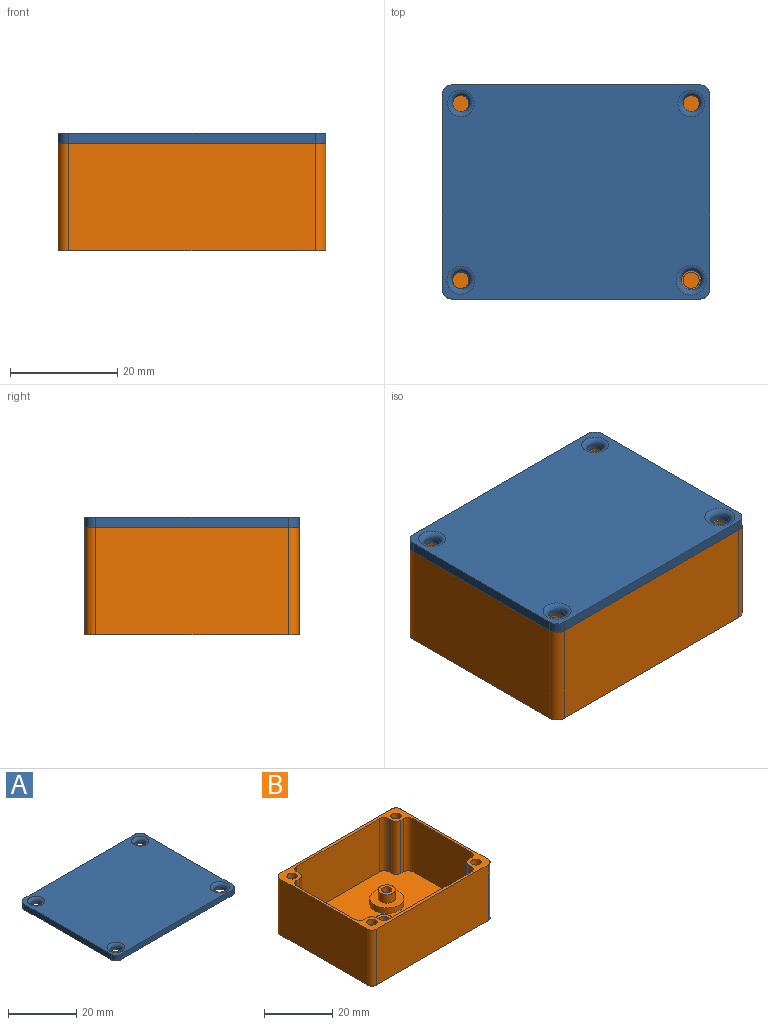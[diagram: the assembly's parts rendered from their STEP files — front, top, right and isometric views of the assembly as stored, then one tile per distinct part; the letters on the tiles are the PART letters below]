
ASSEMBLY  parts=2 mates=1
PART A: 18 faces, bbox 50x40x2 mm
  f0: plane 36x2mm, normal (-1,0,0), area 72mm2, adj f4,f5,f14,f17
  f1: plane 46x2mm, normal (0,-1,0), area 92mm2, adj f4,f5,f14,f15
  f2: plane 36x2mm, normal (1,0,0), area 72mm2, adj f4,f5,f15,f16
  f3: plane 46x2mm, normal (0,1,0), area 92mm2, adj f4,f5,f16,f17
  f4: plane 50x40mm, normal (0,0,1), area 1911mm2, adj f0,f1,f2,f3,f10,f11,f12,f13
  f5: plane 50x40mm, normal (0,0,-1), area 1964mm2, adj f0,f1,f2,f3,f6,f7,f8,f9
  f6: cylinder r=1.5mm len=3mm, axis (0,0,1), area 9.4mm2, adj f5,f13
  f7: cylinder r=1.5mm len=3mm, axis (0,0,1), area 9.4mm2, adj f5,f12
  f8: cylinder r=1.81mm len=3.62mm, axis (0,0,1), area 11.4mm2, adj f5,f11
  f9: cylinder r=1.62mm len=3.23mm, axis (0,0,1), area 10.2mm2, adj f5,f10
  f10: torus R=2.62mm, axis (0,0,1), area 19.5mm2, adj f4,f9
  f11: torus R=2.81mm, axis (0,0,1), area 21.4mm2, adj f4,f8
  f12: torus R=2.5mm, axis (0,0,1), area 18.4mm2, adj f4,f7
  f13: torus R=2.5mm, axis (0,0,1), area 18.4mm2, adj f4,f6
  f14: cylinder r=2mm len=2mm, axis (0,0,-1), area 6.3mm2, adj f0,f1,f4,f5
  f15: cylinder r=2mm len=2mm, axis (0,0,1), area 6.3mm2, adj f1,f2,f4,f5
  f16: cylinder r=2mm len=2mm, axis (0,0,-1), area 6.3mm2, adj f2,f3,f4,f5
  f17: cylinder r=2mm len=2mm, axis (0,0,1), area 6.3mm2, adj f0,f3,f4,f5
PART B: 67 faces, bbox 50x40x20 mm
  f0: cylinder r=1.5mm len=4mm, axis (0,0,-1), area 37.7mm2, adj f30,f50
  f1: cylinder r=1.5mm len=4mm, axis (0,0,-1), area 37.7mm2, adj f32,f43
  f2: plane 48x38mm, normal (0,0,1), area 1563.5mm2, adj f3,f4,f5,f6,f13,f14,f15,f16
  f3: plane 24x19mm, normal (-1,0,0), area 456mm2, adj f2,f7,f60,f61
  f4: plane 34x19mm, normal (0,1,0), area 646mm2, adj f2,f7,f56,f58
  f5: plane 34x19mm, normal (0,-1,0), area 646mm2, adj f2,f7,f62,f64
  f6: plane 24x19mm, normal (1,0,0), area 456mm2, adj f2,f7,f57,f66
  f7: plane 50x40mm, normal (0,0,1), area 247.7mm2, adj f3,f4,f5,f6,f8,f9,f10,f11
  f8: plane 46x20mm, normal (0,1,0), area 920mm2, adj f7,f12,f51,f54
  f9: plane 36x20mm, normal (-1,0,0), area 720mm2, adj f7,f12,f51,f52
  f10: plane 46x20mm, normal (0,-1,0), area 920mm2, adj f7,f12,f52,f53
  f11: plane 36x20mm, normal (1,0,0), area 720mm2, adj f7,f12,f53,f54
  f12: plane 50x40mm, normal (0,0,-1), area 1949.8mm2, adj f8,f9,f10,f11,f37,f38,f39,f40
  f13: plane 19x1mm, normal (0,-1,0), area 19mm2, adj f2,f7,f65,f66
  f14: plane 19x1mm, normal (1,0,0), area 19mm2, adj f2,f7,f64,f65
  f15: plane 19x1mm, normal (0,1,0), area 19mm2, adj f2,f7,f55,f57
  f16: plane 19x1mm, normal (1,0,0), area 19mm2, adj f2,f7,f55,f56
  f17: plane 19x1mm, normal (0,1,0), area 19mm2, adj f2,f7,f59,f60
  f18: plane 19x1mm, normal (-1,0,0), area 19mm2, adj f2,f7,f58,f59
  f19: plane 19x1mm, normal (0,-1,0), area 19mm2, adj f2,f7,f61,f63
  f20: plane 19x1mm, normal (-1,0,0), area 19mm2, adj f2,f7,f62,f63
  f21: cylinder r=1.5mm len=10mm, axis (0,0,1), area 94.2mm2, adj f7,f22
  f22: plane 3x3mm, normal (0,0,1), area 7.1mm2, adj f21
  f23: cylinder r=1.5mm len=10mm, axis (0,0,1), area 94.2mm2, adj f7,f24
  f24: plane 3x3mm, normal (0,0,1), area 7.1mm2, adj f23
  f25: cylinder r=1.5mm len=10mm, axis (0,0,1), area 94.2mm2, adj f7,f26
  f26: plane 3x3mm, normal (0,0,1), area 7.1mm2, adj f25
  f27: cylinder r=1.5mm len=10mm, axis (0,0,1), area 94.2mm2, adj f7,f28
  f28: plane 3x3mm, normal (0,0,1), area 7.1mm2, adj f27
  f29: cylinder r=2.5mm len=5mm, axis (0,0,-1), area 47.1mm2, adj f30,f34
  f30: plane 5x5mm, normal (0,0,1), area 12.6mm2, adj f0,f29
  f31: cylinder r=2.5mm len=5mm, axis (0,0,-1), area 47.1mm2, adj f32,f36
  f32: plane 5x5mm, normal (0,0,1), area 12.6mm2, adj f1,f31
  f33: cylinder r=5mm len=10mm, axis (0,0,-1), area 62.8mm2, adj f2,f34
  f34: plane 10x10mm, normal (0,0,1), area 58.9mm2, adj f29,f33
  f35: cylinder r=5mm len=10mm, axis (0,0,-1), area 62.8mm2, adj f2,f36
  f36: plane 10x10mm, normal (0,0,1), area 58.9mm2, adj f31,f35
  f37: plane 2.25x2mm, normal (0.75,-0.66,0), area 6mm2, adj f12,f38,f42,f43
  f38: plane 2.94x2mm, normal (-0.2,-0.98,0), area 6mm2, adj f12,f37,f39,f43
  f39: plane 2.85x2mm, normal (-0.95,-0.32,0), area 6mm2, adj f12,f38,f40,f43
  f40: plane 2.25x2mm, normal (-0.75,0.66,0), area 6mm2, adj f12,f39,f41,f43
  f41: plane 2.94x2mm, normal (0.2,0.98,0), area 6mm2, adj f12,f40,f42,f43
  f42: plane 2.85x2mm, normal (0.95,0.32,0), area 6mm2, adj f12,f37,f41,f43
  f43: plane 5.88x5.69mm, normal (0,0,-1), area 16.3mm2, adj f1,f37,f38,f39,f40,f41,f42
  f44: plane 2.55x2mm, normal (-0.85,-0.53,0), area 6mm2, adj f12,f45,f49,f50
  f45: plane 2.65x2mm, normal (-0.88,0.47,0), area 6mm2, adj f12,f44,f46,f50
  f46: plane 3x2mm, normal (-0.03,1,0), area 6mm2, adj f12,f45,f47,f50
  f47: plane 2.55x2mm, normal (0.85,0.53,0), area 6mm2, adj f12,f46,f48,f50
  f48: plane 2.65x2mm, normal (0.88,-0.47,0), area 6mm2, adj f12,f47,f49,f50
  f49: plane 3x2mm, normal (0.03,-1,0), area 6mm2, adj f12,f44,f48,f50
  f50: plane 6x5.29mm, normal (0,0,-1), area 16.3mm2, adj f0,f44,f45,f46,f47,f48,f49
  f51: cylinder r=2mm len=20mm, axis (0,0,1), area 62.8mm2, adj f7,f8,f9,f12
  f52: cylinder r=2mm len=20mm, axis (0,0,-1), area 62.8mm2, adj f7,f9,f10,f12
  f53: cylinder r=2mm len=20mm, axis (0,0,1), area 62.8mm2, adj f7,f10,f11,f12
  f54: cylinder r=2mm len=20mm, axis (0,0,-1), area 62.8mm2, adj f7,f8,f11,f12
  f55: cylinder r=2mm len=19mm, axis (0,0,1), area 59.7mm2, adj f2,f7,f15,f16
  f56: cylinder r=2mm len=19mm, axis (0,0,1), area 59.7mm2, adj f2,f4,f7,f16
  f57: cylinder r=2mm len=19mm, axis (0,0,-1), area 59.7mm2, adj f2,f6,f7,f15
  f58: cylinder r=2mm len=19mm, axis (0,0,-1), area 59.7mm2, adj f2,f4,f7,f18
  f59: cylinder r=2mm len=19mm, axis (0,0,1), area 59.7mm2, adj f2,f7,f17,f18
  f60: cylinder r=2mm len=19mm, axis (0,0,-1), area 59.7mm2, adj f2,f3,f7,f17
  f61: cylinder r=2mm len=19mm, axis (0,0,1), area 59.7mm2, adj f2,f3,f7,f19
  f62: cylinder r=2mm len=19mm, axis (0,0,-1), area 59.7mm2, adj f2,f5,f7,f20
  f63: cylinder r=2mm len=19mm, axis (0,0,1), area 59.7mm2, adj f2,f7,f19,f20
  f64: cylinder r=2mm len=19mm, axis (0,0,1), area 59.7mm2, adj f2,f5,f7,f14
  f65: cylinder r=2mm len=19mm, axis (0,0,1), area 59.7mm2, adj f2,f7,f13,f14
  f66: cylinder r=2mm len=19mm, axis (0,0,1), area 59.7mm2, adj f2,f6,f7,f13
PLACE A t=(-11.02,-11.9,-17.09)mm
PLACE B rot(axis=(0,0,-1),0deg) t=(43.39,-9.69,-37.09)mm
MATE slider B.f25 <-> A.f8  axis (0,0,1) through (38,-4.81,-17.09)mm
